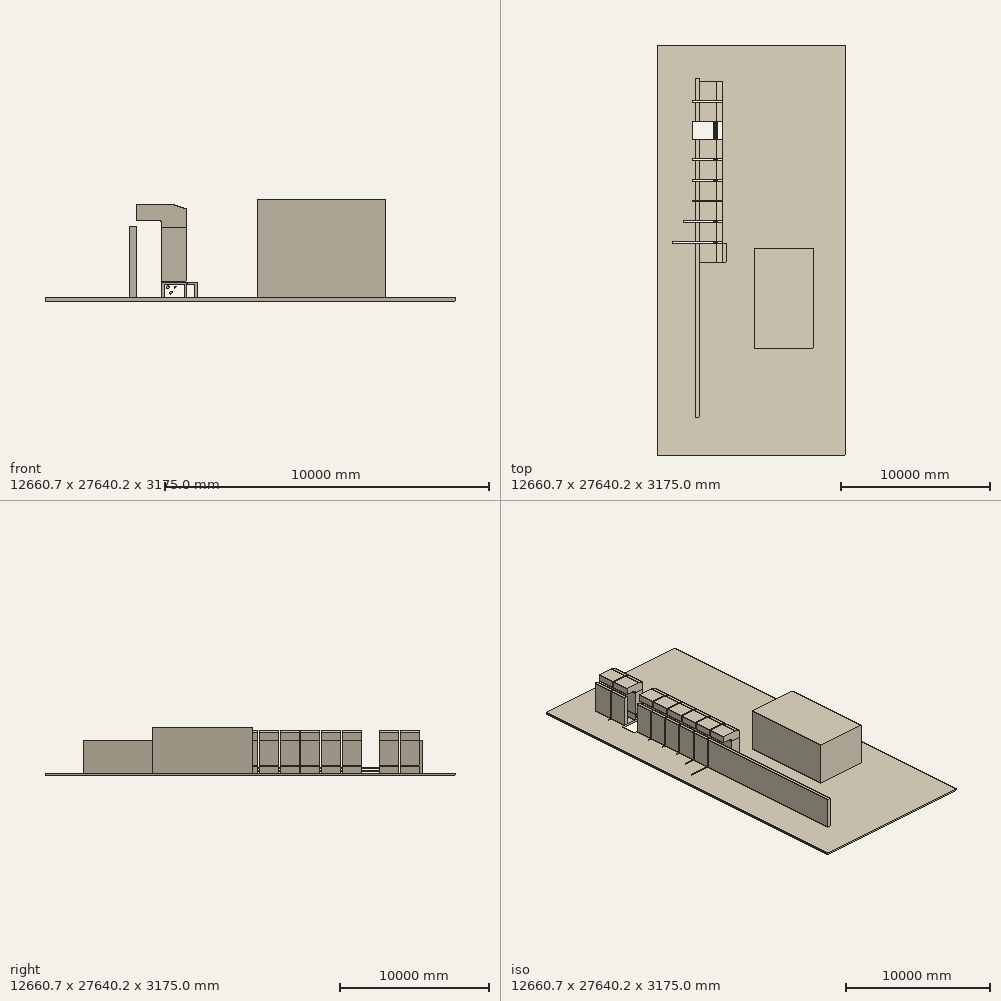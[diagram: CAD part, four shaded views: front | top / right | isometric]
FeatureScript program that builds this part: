
annotation { "Feature Type Name" : "Feature", "Feature Type Description" : "" }
export const myFeature = defineFeature(function(context is Context, id is Id, definition is map)
    precondition{}
    {
        {
            var Q0;
            Q0=qCreatedBy(makeId("Top.planeOp"),FACE);
            var sketch = newSketch(context, id + "F0", { "sketchPlane" : qUnion([Q0])});
            skLineSegment(sketch, "E0.bottom", {"start": v(0, 0) * mm, "end": v(3962.4, 0) * mm});
            skLineSegment(sketch, "E0.top", {"start": v(0, 9040.37) * mm, "end": v(100.58, 9040.37) * mm});
            skLineSegment(sketch, "E0.left", {"start": v(0, 0) * mm, "end": v(0, 9040.37) * mm});
            skLineSegment(sketch, "E0.right", {"start": v(3962.4, 0) * mm, "end": v(3962.4, 100.58) * mm});
            skLineSegment(sketch, "E1.bottom", {"start": v(0, -9144) * mm, "end": v(3962.4, -9144) * mm});
            skLineSegment(sketch, "E1.top", {"start": v(0, -2438.4) * mm, "end": v(3962.4, -2438.4) * mm});
            skLineSegment(sketch, "E1.left", {"start": v(0, -2438.4) * mm, "end": v(0, -9144) * mm});
            skLineSegment(sketch, "E1.right", {"start": v(3962.4, -2438.4) * mm, "end": v(3962.4, -9144) * mm});
            skLineSegment(sketch, "E2", {"start": v(100.58, 9040.37) * mm, "end": v(100.58, 100.58) * mm});
            skLineSegment(sketch, "E3", {"start": v(100.58, 100.58) * mm, "end": v(3962.4, 100.58) * mm});
            skSolve(sketch);
        }
        {
            var Q0;
            Q0=qSketchRegion(id+"F0",true);
            extrude(context, id + "F1", {"entities" : qUnion([Q0]), "depth" : 3048 * mm});
        }
        {
            var Q0;
            Q0=qCreatedBy(makeId("Top.planeOp"),FACE);
            var sketch = newSketch(context, id + "F2", { "sketchPlane" : qUnion([Q0])});
            skLineSegment(sketch, "E4.bottom", {"start": v(-3718.56, 9040.37) * mm, "end": v(3962.4, 9040.37) * mm});
            skLineSegment(sketch, "E4.top", {"start": v(-3718.56, 9284.2) * mm, "end": v(3962.4, 9284.2) * mm});
            skLineSegment(sketch, "E4.left", {"start": v(-3718.56, 9040.37) * mm, "end": v(-3718.56, 9284.2) * mm});
            skLineSegment(sketch, "E4.right", {"start": v(3962.4, 9040.37) * mm, "end": v(3962.4, 9284.2) * mm});
            skLineSegment(sketch, "E5.bottom", {"start": v(-3718.56, 9040.37) * mm, "end": v(-3962.4, 9040.37) * mm});
            skLineSegment(sketch, "E5.top", {"start": v(-3718.56, -13819.63) * mm, "end": v(-3962.4, -13819.63) * mm});
            skLineSegment(sketch, "E5.left", {"start": v(-3718.56, 9040.37) * mm, "end": v(-3718.56, -13819.63) * mm});
            skLineSegment(sketch, "E5.right", {"start": v(-3962.4, 9040.37) * mm, "end": v(-3962.4, -13819.63) * mm});
            skSolve(sketch);
        }
        {
            var Q0;
            Q0=qSketchRegion(id+"F2",true);
            extrude(context, id + "F3", {"entities" : qUnion([Q0]), "depth" : 2212.85 * mm});
        }
        {
            var Q0;
            Q0=makeQuery(id+"F1.opExtrude","CAP_FACE",FACE,{"disambiguationData":[OSD([sQuery(id+"F0.wireOp",EDGE,"E0.bottom"),sQuery(id+"F0.wireOp",EDGE,"E0.top"),sQuery(id+"F0.wireOp",EDGE,"E0.left"),sQuery(id+"F0.wireOp",EDGE,"E0.right")])],"isStart":false});
            var sketch = newSketch(context, id + "F4", { "sketchPlane" : qUnion([Q0])});
            skLineSegment(sketch, "E6.bottom", {"start": v(3962.4, 9284.2) * mm, "end": v(-2990.09, 9284.2) * mm});
            skLineSegment(sketch, "E6.top", {"start": v(3962.4, -10436.35) * mm, "end": v(-2990.09, -10436.35) * mm});
            skLineSegment(sketch, "E6.left", {"start": v(3962.4, 9284.2) * mm, "end": v(3962.4, -10436.35) * mm});
            skLineSegment(sketch, "E6.right", {"start": v(-2990.09, 9284.2) * mm, "end": v(-2990.09, -10436.35) * mm});
            skSolve(sketch);
        }
        {
            var Q0;
            Q0=qSketchRegion(id+"F4",true);
            extrude(context, id + "F5", {"entities" : qUnion([Q0]), "depth" : 1270 * mm});
        }
        {
            var Q0;
            Q0=makeQuery(id+"F1.opExtrude","SWEPT_FACE",FACE,{"disambiguationData":[OSD([sQuery(id+"F0.wireOp",EDGE,"E1.right")])]});
            var sketch = newSketch(context, id + "F6", { "sketchPlane" : qUnion([Q0])});
            skLineSegment(sketch, "E7.bottom", {"start": v(-9144, 0) * mm, "end": v(9284.2, 0) * mm});
            skLineSegment(sketch, "E7.top", {"start": v(-9144, 4318) * mm, "end": v(9284.2, 4318) * mm});
            skLineSegment(sketch, "E7.left", {"start": v(-9144, 0) * mm, "end": v(-9144, 3048) * mm});
            skLineSegment(sketch, "E7.right", {"start": v(9284.2, 0) * mm, "end": v(9284.2, 4318) * mm});
            skLineSegment(sketch, "E8.bottom", {"start": v(-9144, 4318) * mm, "end": v(-10436.35, 4318) * mm});
            skLineSegment(sketch, "E8.top", {"start": v(-9144, 3048) * mm, "end": v(-10436.35, 3048) * mm});
            skLineSegment(sketch, "E8.right", {"start": v(-10436.35, 4318) * mm, "end": v(-10436.35, 3048) * mm});
            skSolve(sketch);
        }
        {
            var Q0;
            Q0=qSketchRegion(id+"F6",true);
            extrude(context, id + "F7", {"entities" : qUnion([Q0]), "depth" : 1270 * mm});
        }
        {
            var Q0;
            Q0=qCreatedBy(makeId("Top.planeOp"),FACE);
            var sketch = newSketch(context, id + "F8", { "sketchPlane" : qUnion([Q0])});
            skLineSegment(sketch, "E9.bottom", {"start": v(6117.86, 11268.55) * mm, "end": v(-6542.87, 11268.55) * mm});
            skLineSegment(sketch, "E9.top", {"start": v(6117.86, -16371.62) * mm, "end": v(-6542.87, -16371.62) * mm});
            skLineSegment(sketch, "E9.left", {"start": v(6117.86, 11268.55) * mm, "end": v(6117.86, -16371.62) * mm});
            skLineSegment(sketch, "E9.right", {"start": v(-6542.87, 11268.55) * mm, "end": v(-6542.87, -16371.62) * mm});
            skSolve(sketch);
        }
        {
            var Q0;
            Q0=qSketchRegion(id+"F8",true);
            extrude(context, id + "F9", {"entities" : qUnion([Q0]), "oppositeDirection" : true, "depth" : 127 * mm});
        }
        {
            var Q0;
            Q0=makeQuery(id+"F3.opExtrude","CAP_FACE",FACE,{"disambiguationData":[OSD([sQuery(id+"F2.wireOp",EDGE,"E4.bottom"),sQuery(id+"F2.wireOp",EDGE,"E4.top"),sQuery(id+"F2.wireOp",EDGE,"E4.left"),sQuery(id+"F2.wireOp",EDGE,"E4.right")])],"isStart":false});
            var sketch = newSketch(context, id + "F10", { "sketchPlane" : qUnion([Q0])});
            skLineSegment(sketch, "E10.bottom", {"start": v(-3718.56, 9284.2) * mm, "end": v(3962.4, 9284.2) * mm});
            skLineSegment(sketch, "E10.top", {"start": v(-3718.56, 9040.37) * mm, "end": v(3962.4, 9040.37) * mm});
            skLineSegment(sketch, "E10.left", {"start": v(-3718.56, 9284.2) * mm, "end": v(-3718.56, 9040.37) * mm});
            skLineSegment(sketch, "E10.right", {"start": v(3962.4, 9284.2) * mm, "end": v(3962.4, 9040.37) * mm});
            skSolve(sketch);
        }
        {
            var Q0;
            Q0=qSketchRegion(id+"F10",true);
            var Q1;
            Q1=makeQuery(id+"F5.opExtrude","CAP_FACE",FACE,{"disambiguationData":[OSD([sQuery(id+"F4.wireOp",EDGE,"E6.bottom"),sQuery(id+"F4.wireOp",EDGE,"E6.top"),sQuery(id+"F4.wireOp",EDGE,"E6.left"),sQuery(id+"F4.wireOp",EDGE,"E6.right")])],"isStart":false});
            extrude(context, id + "F11", {"entities" : qUnion([Q0]), "operationType" : NewBodyOperationType.ADD, "endBound" : BoundingType.UP_TO_SURFACE, "endBoundEntityFace" : qUnion([Q1]), "depth" : 25.4 * mm});
        }
        {
            var Q0;
            Q0=qCreatedBy(makeId("Top.planeOp"),FACE);
            var sketch = newSketch(context, id + "F12", { "sketchPlane" : qUnion([Q0])});
            skLineSegment(sketch, "E11.bottom", {"start": v(-2956.56, -560.83) * mm, "end": v(-2181.86, -560.83) * mm});
            skLineSegment(sketch, "E11.top", {"start": v(-2956.56, 734.57) * mm, "end": v(-2181.86, 734.57) * mm});
            skLineSegment(sketch, "E11.left", {"start": v(-2956.56, -560.83) * mm, "end": v(-2956.56, 734.57) * mm});
            skLineSegment(sketch, "E11.right", {"start": v(-2181.86, -560.83) * mm, "end": v(-2181.86, 734.57) * mm});
            skLineSegment(sketch, "E12.bottom", {"start": v(-2956.56, 836.17) * mm, "end": v(-2181.86, 836.17) * mm});
            skLineSegment(sketch, "E12.top", {"start": v(-2956.56, 2131.57) * mm, "end": v(-2181.86, 2131.57) * mm});
            skLineSegment(sketch, "E12.left", {"start": v(-2956.56, 836.17) * mm, "end": v(-2956.56, 2131.57) * mm});
            skLineSegment(sketch, "E12.right", {"start": v(-2181.86, 836.17) * mm, "end": v(-2181.86, 2131.57) * mm});
            skLineSegment(sketch, "E13.bottom", {"start": v(-2956.56, 2233.17) * mm, "end": v(-2181.86, 2233.17) * mm});
            skLineSegment(sketch, "E13.top", {"start": v(-2956.56, 3528.57) * mm, "end": v(-2181.86, 3528.57) * mm});
            skLineSegment(sketch, "E13.left", {"start": v(-2956.56, 2233.17) * mm, "end": v(-2956.56, 3528.57) * mm});
            skLineSegment(sketch, "E13.right", {"start": v(-2181.86, 2233.17) * mm, "end": v(-2181.86, 3528.57) * mm});
            skLineSegment(sketch, "E14.bottom", {"start": v(-2956.56, 8837.17) * mm, "end": v(-2181.86, 8837.17) * mm});
            skLineSegment(sketch, "E14.top", {"start": v(-2956.56, 7541.77) * mm, "end": v(-2181.86, 7541.77) * mm});
            skLineSegment(sketch, "E14.left", {"start": v(-2956.56, 8837.17) * mm, "end": v(-2956.56, 7541.77) * mm});
            skLineSegment(sketch, "E14.right", {"start": v(-2181.86, 8837.17) * mm, "end": v(-2181.86, 7541.77) * mm});
            skLineSegment(sketch, "E15.bottom", {"start": v(-2956.56, 7440.17) * mm, "end": v(-2181.86, 7440.17) * mm});
            skLineSegment(sketch, "E15.top", {"start": v(-2956.56, 6144.77) * mm, "end": v(-2181.86, 6144.77) * mm});
            skLineSegment(sketch, "E15.left", {"start": v(-2956.56, 7440.17) * mm, "end": v(-2956.56, 6144.77) * mm});
            skLineSegment(sketch, "E15.right", {"start": v(-2181.86, 7440.17) * mm, "end": v(-2181.86, 6144.77) * mm});
            skLineSegment(sketch, "E16.bottom", {"start": v(-2956.56, 4925.57) * mm, "end": v(-2181.86, 4925.57) * mm});
            skLineSegment(sketch, "E16.top", {"start": v(-2956.56, 3630.17) * mm, "end": v(-2181.86, 3630.17) * mm});
            skLineSegment(sketch, "E16.left", {"start": v(-2956.56, 4925.57) * mm, "end": v(-2956.56, 3630.17) * mm});
            skLineSegment(sketch, "E16.right", {"start": v(-2181.86, 4925.57) * mm, "end": v(-2181.86, 3630.17) * mm});
            skLineSegment(sketch, "E17", {"start": v(-2956.56, 2131.57) * mm, "end": v(-2956.56, 2233.17) * mm, "construction": true});
            skLineSegment(sketch, "E18", {"start": v(-2956.56, 734.57) * mm, "end": v(-2956.56, 836.17) * mm, "construction": true});
            skLineSegment(sketch, "E19", {"start": v(-2956.56, 3528.57) * mm, "end": v(-2956.56, 3630.17) * mm, "construction": true});
            skLineSegment(sketch, "E20", {"start": v(-2956.56, 7440.17) * mm, "end": v(-2956.56, 7541.77) * mm, "construction": true});
            skLineSegment(sketch, "E21.bottom", {"start": v(-2956.56, -662.43) * mm, "end": v(-2181.86, -662.43) * mm});
            skLineSegment(sketch, "E21.top", {"start": v(-2956.56, -1957.83) * mm, "end": v(-2181.86, -1957.83) * mm});
            skLineSegment(sketch, "E21.left", {"start": v(-2956.56, -662.43) * mm, "end": v(-2956.56, -1957.83) * mm});
            skLineSegment(sketch, "E21.right", {"start": v(-2181.86, -662.43) * mm, "end": v(-2181.86, -1957.83) * mm});
            skLineSegment(sketch, "E22.bottom", {"start": v(-2956.56, -2059.43) * mm, "end": v(-2181.86, -2059.43) * mm});
            skLineSegment(sketch, "E22.top", {"start": v(-2956.56, -3354.83) * mm, "end": v(-2181.86, -3354.83) * mm});
            skLineSegment(sketch, "E22.left", {"start": v(-2956.56, -2059.43) * mm, "end": v(-2956.56, -3354.83) * mm});
            skLineSegment(sketch, "E22.right", {"start": v(-2181.86, -2059.43) * mm, "end": v(-2181.86, -3354.83) * mm});
            skLineSegment(sketch, "E23", {"start": v(-2956.56, -662.43) * mm, "end": v(-2956.56, -560.83) * mm, "construction": true});
            skLineSegment(sketch, "E24", {"start": v(-2956.56, -2059.43) * mm, "end": v(-2956.56, -1957.83) * mm, "construction": true});
            skSolve(sketch);
        }
        {
            var Q0;
            Q0=qSketchRegion(id+"F12",true);
            extrude(context, id + "F13", {"entities" : qUnion([Q0]), "depth" : 2184.4 * mm});
        }
        {
            var Q0;
            Q0=qCreatedBy(makeId("Top.planeOp"),FACE);
            var sketch = newSketch(context, id + "F14", { "sketchPlane" : qUnion([Q0])});
            skLineSegment(sketch, "E25.bottom", {"start": v(607.65, 7254.54) * mm, "end": v(3668.35, 7254.54) * mm});
            skLineSegment(sketch, "E25.top", {"start": v(607.65, 5165.39) * mm, "end": v(3668.35, 5165.39) * mm});
            skLineSegment(sketch, "E25.left", {"start": v(607.65, 7254.54) * mm, "end": v(607.65, 5165.39) * mm});
            skLineSegment(sketch, "E25.right", {"start": v(3668.35, 7254.54) * mm, "end": v(3668.35, 5165.39) * mm});
            skSolve(sketch);
        }
        {
            var Q0;
            Q0=qSketchRegion(id+"F14",true);
            extrude(context, id + "F15", {"entities" : qUnion([Q0]), "depth" : 1739.9 * mm});
        }
        {
            var Q0;
            Q0=qCreatedBy(makeId("Top.planeOp"),FACE);
            var sketch = newSketch(context, id + "F16", { "sketchPlane" : qUnion([Q0])});
            skLineSegment(sketch, "E26.bottom", {"start": v(1227.74, 8964) * mm, "end": v(478.44, 8964) * mm});
            skLineSegment(sketch, "E26.top", {"start": v(1227.74, 7363.8) * mm, "end": v(478.44, 7363.8) * mm});
            skLineSegment(sketch, "E26.left", {"start": v(1227.74, 8964) * mm, "end": v(1227.74, 7363.8) * mm});
            skLineSegment(sketch, "E26.right", {"start": v(478.44, 8964) * mm, "end": v(478.44, 7363.8) * mm});
            skSolve(sketch);
        }
        {
            var Q0;
            Q0=qSketchRegion(id+"F16",true);
            extrude(context, id + "F17", {"entities" : qUnion([Q0]), "depth" : 1447.8 * mm});
        }
        {
            var Q0;
            Q0=makeQuery(id+"F13.opExtrude","SWEPT_FACE",FACE,{"disambiguationData":[OSD([sQuery(id+"F12.wireOp",EDGE,"E22.top")])]});
            var sketch = newSketch(context, id + "F18", { "sketchPlane" : qUnion([Q0])});
            skLineSegment(sketch, "E27", {"start": v(-2956.56, 2184.4) * mm, "end": v(-2956.56, 2324.1) * mm});
            skLineSegment(sketch, "E28", {"start": v(-2956.56, 2324.1) * mm, "end": v(-3020.06, 2387.6) * mm});
            skLineSegment(sketch, "E29", {"start": v(-3020.06, 2387.6) * mm, "end": v(-3045.46, 2387.6) * mm});
            skLineSegment(sketch, "E30", {"start": v(-3045.46, 2387.6) * mm, "end": v(-3045.46, 2870.2) * mm, "construction": true});
            skLineSegment(sketch, "E31", {"start": v(-3045.46, 2870.2) * mm, "end": v(-2569.2, 2870.2) * mm});
            skLineSegment(sketch, "E32", {"start": v(-2569.2, 2870.2) * mm, "end": v(-2181.86, 2743.2) * mm});
            skLineSegment(sketch, "E33", {"start": v(-2181.86, 2743.2) * mm, "end": v(-2181.86, 2184.4) * mm});
            skLineSegment(sketch, "E34", {"start": v(-2181.86, 2184.4) * mm, "end": v(-2956.56, 2184.4) * mm});
            skLineSegment(sketch, "E35", {"start": v(-2569.2, 2870.2) * mm, "end": v(-2569.2, 2184.4) * mm, "construction": true});
            skLineSegment(sketch, "E36", {"start": v(-3045.46, 2387.6) * mm, "end": v(-3743.96, 2387.6) * mm});
            skLineSegment(sketch, "E37", {"start": v(-3743.96, 2387.6) * mm, "end": v(-3743.96, 2870.2) * mm});
            skLineSegment(sketch, "E38", {"start": v(-3743.96, 2870.2) * mm, "end": v(-3045.46, 2870.2) * mm});
            skSolve(sketch);
        }
        {
            var Q0;
            Q0 = qSketchRegion(id + "F18", true);
            var Q1;
            Q1=makeQuery(id+"F13.opExtrude","SWEPT_FACE",FACE,{"disambiguationData":[OSD([sQuery(id+"F12.wireOp",EDGE,"E14.bottom")])]});
            extrude(context, id + "F19", {"entities" : qUnion([Q0]), "endBound" : BoundingType.UP_TO_SURFACE, "oppositeDirection" : true, "endBoundEntityFace" : qUnion([Q1]), "depth" : 25.4 * mm});
        }
        {
            var Q0;
            Q0=makeQuery(id+"F19.opExtrude","SWEPT_FACE",FACE,{"disambiguationData":[OSD([sQuery(id+"F18.wireOp",EDGE,"E31"),sQuery(id+"F18.wireOp",EDGE,"zUbst6hV-jxuJ-IhWM-silx-YQ4qEfQ2v0dv")])]});
            var sketch = newSketch(context, id + "F20", { "sketchPlane" : qUnion([Q0])});
            skLineSegment(sketch, "E39.1", {"start": v(-2956.56, 734.57) * mm, "end": v(-2181.86, 734.57) * mm});
            skLineSegment(sketch, "E39.4", {"start": v(-2956.56, 836.17) * mm, "end": v(-2181.86, 836.17) * mm});
            skLineSegment(sketch, "E39.5", {"start": v(-2956.56, 2131.57) * mm, "end": v(-2181.86, 2131.57) * mm});
            skLineSegment(sketch, "E39.8", {"start": v(-2956.56, 2233.17) * mm, "end": v(-2181.86, 2233.17) * mm});
            skLineSegment(sketch, "E39.9", {"start": v(-2956.56, 3528.57) * mm, "end": v(-2181.86, 3528.57) * mm});
            skLineSegment(sketch, "E39.12", {"start": v(-2956.56, 8837.17) * mm, "end": v(-2181.86, 8837.17) * mm});
            skLineSegment(sketch, "E39.13", {"start": v(-2956.56, 7541.77) * mm, "end": v(-2181.86, 7541.77) * mm});
            skLineSegment(sketch, "E39.16", {"start": v(-2956.56, 7440.17) * mm, "end": v(-2181.86, 7440.17) * mm});
            skLineSegment(sketch, "E39.17", {"start": v(-2956.56, 6144.77) * mm, "end": v(-2181.86, 6144.77) * mm});
            skLineSegment(sketch, "E39.20", {"start": v(-2956.56, 4925.57) * mm, "end": v(-2181.86, 4925.57) * mm});
            skLineSegment(sketch, "E39.21", {"start": v(-2956.56, 3630.17) * mm, "end": v(-2181.86, 3630.17) * mm});
            skLineSegment(sketch, "E40", {"start": v(-2956.56, 734.57) * mm, "end": v(-4216.86, 734.57) * mm});
            skLineSegment(sketch, "E41", {"start": v(-4216.86, 734.57) * mm, "end": v(-4216.86, 836.17) * mm});
            skLineSegment(sketch, "E42", {"start": v(-4216.86, 836.17) * mm, "end": v(-2956.56, 836.17) * mm});
            skLineSegment(sketch, "E43", {"start": v(-2181.86, 734.57) * mm, "end": v(-2181.86, 836.17) * mm});
            skLineSegment(sketch, "E44", {"start": v(-2956.56, 2131.57) * mm, "end": v(-4216.86, 2131.57) * mm});
            skLineSegment(sketch, "E45", {"start": v(-4216.86, 2131.57) * mm, "end": v(-4216.86, 2233.17) * mm});
            skLineSegment(sketch, "E46", {"start": v(-4216.86, 2233.17) * mm, "end": v(-2956.56, 2233.17) * mm});
            skLineSegment(sketch, "E47", {"start": v(-2181.86, 2131.57) * mm, "end": v(-2181.86, 2233.17) * mm});
            skLineSegment(sketch, "E48", {"start": v(-2181.86, 3528.57) * mm, "end": v(-2181.86, 3630.17) * mm});
            skLineSegment(sketch, "E49", {"start": v(-2181.86, 4925.57) * mm, "end": v(-2181.86, 6144.77) * mm});
            skLineSegment(sketch, "E50", {"start": v(-2181.86, 7440.17) * mm, "end": v(-2181.86, 7541.77) * mm});
            skLineSegment(sketch, "E51", {"start": v(-2956.56, 3528.57) * mm, "end": v(-4216.86, 3528.57) * mm});
            skLineSegment(sketch, "E52", {"start": v(-4216.86, 3528.57) * mm, "end": v(-4216.86, 3630.17) * mm});
            skLineSegment(sketch, "E53", {"start": v(-4216.86, 3630.17) * mm, "end": v(-2956.56, 3630.17) * mm});
            skLineSegment(sketch, "E54", {"start": v(-2956.56, 4925.57) * mm, "end": v(-4216.86, 4925.57) * mm});
            skLineSegment(sketch, "E55", {"start": v(-4216.86, 4925.57) * mm, "end": v(-4216.86, 6144.77) * mm});
            skLineSegment(sketch, "E56", {"start": v(-4216.86, 6144.77) * mm, "end": v(-2956.56, 6144.77) * mm});
            skLineSegment(sketch, "E57", {"start": v(-2956.56, 7440.17) * mm, "end": v(-4216.86, 7440.17) * mm});
            skLineSegment(sketch, "E58", {"start": v(-4216.86, 7440.17) * mm, "end": v(-4216.86, 7541.77) * mm});
            skLineSegment(sketch, "E59", {"start": v(-4216.86, 7541.77) * mm, "end": v(-2956.56, 7541.77) * mm});
            skLineSegment(sketch, "E60.bottom", {"start": v(-2181.86, -560.83) * mm, "end": v(-4784.94, -560.83) * mm});
            skLineSegment(sketch, "E60.top", {"start": v(-2181.86, -662.43) * mm, "end": v(-4784.94, -662.43) * mm});
            skLineSegment(sketch, "E60.left", {"start": v(-2181.86, -560.83) * mm, "end": v(-2181.86, -662.43) * mm});
            skLineSegment(sketch, "E60.right", {"start": v(-4784.94, -560.83) * mm, "end": v(-4784.94, -662.43) * mm});
            skLineSegment(sketch, "E61.bottom", {"start": v(-2181.86, -1957.83) * mm, "end": v(-5549.38, -1957.83) * mm});
            skLineSegment(sketch, "E61.top", {"start": v(-2181.86, -2059.43) * mm, "end": v(-5549.38, -2059.43) * mm});
            skLineSegment(sketch, "E61.left", {"start": v(-2181.86, -1957.83) * mm, "end": v(-2181.86, -2059.43) * mm});
            skLineSegment(sketch, "E61.right", {"start": v(-5549.38, -1957.83) * mm, "end": v(-5549.38, -2059.43) * mm});
            skSolve(sketch);
        }
        {
            var Q0;
            Q0 = qSketchRegion(id + "F20", true);
            extrude(context, id + "F21", {"entities" : qUnion([Q0]), "operationType" : NewBodyOperationType.REMOVE, "endBound" : BoundingType.THROUGH_ALL, "oppositeDirection" : true, "depth" : 25.4 * mm});
        }
        {
            var Q0;
            Q0=qCreatedBy(makeId("Top.planeOp"),FACE);
            var sketch = newSketch(context, id + "F22", { "sketchPlane" : qUnion([Q0])});
            skSolve(sketch);
        }
        {
            var Q0;
            Q0 = qSketchRegion(id + "F22", true);
            var Q1;
            Q1=makeQuery(id+"F5.opExtrude","CAP_FACE",FACE,{"disambiguationData":[OSD([sQuery(id+"F4.wireOp",EDGE,"E6.bottom"),sQuery(id+"F4.wireOp",EDGE,"E6.top"),sQuery(id+"F4.wireOp",EDGE,"E6.left"),sQuery(id+"F4.wireOp",EDGE,"E6.right")])],"isStart":false});
            extrude(context, id + "F23", {"entities" : qUnion([Q0, Q1]), "depth" : 25.4 * mm});
        }
        {
            var Q0;
            Q0=makeQuery(id+"F13.opExtrude","SWEPT_FACE",FACE,{"disambiguationData":[OSD([sQuery(id+"F12.wireOp",EDGE,"E22.top")])]});
            var sketch = newSketch(context, id + "F24", { "sketchPlane" : qUnion([Q0])});
            skLineSegment(sketch, "E62.bottom", {"start": v(-2956.56, 488.95) * mm, "end": v(-2181.86, 488.95) * mm});
            skLineSegment(sketch, "E62.top", {"start": v(-2956.56, 482.6) * mm, "end": v(-2181.86, 482.6) * mm});
            skLineSegment(sketch, "E62.left", {"start": v(-2956.56, 488.95) * mm, "end": v(-2956.56, 482.6) * mm});
            skLineSegment(sketch, "E62.right", {"start": v(-2181.86, 488.95) * mm, "end": v(-2181.86, 482.6) * mm});
            skLineSegment(sketch, "E63.bottom", {"start": v(-2880.36, 406.4) * mm, "end": v(-2258.06, 406.4) * mm});
            skLineSegment(sketch, "E63.top", {"start": v(-2880.36, 0) * mm, "end": v(-2258.06, 0) * mm});
            skLineSegment(sketch, "E63.left", {"start": v(-2880.36, 406.4) * mm, "end": v(-2880.36, 0) * mm});
            skLineSegment(sketch, "E63.right", {"start": v(-2258.06, 406.4) * mm, "end": v(-2258.06, 0) * mm});
            skSolve(sketch);
        }
        {
            var Q0;
            Q0 = qSketchRegion(id + "F24", true);
            var Q1;
            Q1=makeQuery(id+"F13.opExtrude","SWEPT_FACE",FACE,{"disambiguationData":[OSD([sQuery(id+"F12.wireOp",EDGE,"E14.bottom")])]});
            extrude(context, id + "F25", {"entities" : qUnion([Q0]), "operationType" : NewBodyOperationType.REMOVE, "endBound" : BoundingType.UP_TO_SURFACE, "oppositeDirection" : true, "endBoundEntityFace" : qUnion([Q1]), "depth" : 25.4 * mm});
        }
        {
            var Q0;
            {var subQ2=sQuery(id+"F12.wireOp",EDGE,"E22.top");Q0=makeQuery(id+"F25.boolean.opBoolean","SPLIT",FACE,{"disambiguationData":[TD([makeQuery(id+"F25.opExtrude","SWEPT_FACE",FACE,{"disambiguationData":[OSD([sQuery(id+"F24.wireOp",EDGE,"E62.top")])]})])],"derivedFrom":makeQuery(id+"F13.opExtrude","SWEPT_FACE",FACE,{"disambiguationData":[OSD([subQ2])]})});}
            var sketch = newSketch(context, id + "F26", { "sketchPlane" : qUnion([Q0])});
            skCircle(sketch, "E64", {"center": v(-2755.23, 325.58) * mm, "radius": 44.3 * mm});
            skCircle(sketch, "E65", {"center": v(-2532.33, 324.26) * mm, "radius": 26.75 * mm});
            skCircle(sketch, "E66", {"center": v(-2659.35, 151) * mm, "radius": 40.42 * mm});
            skSolve(sketch);
        }
        {
            var Q0;
            Q0 = qSketchRegion(id + "F26", true);
            extrude(context, id + "F27", {"entities" : qUnion([Q0]), "oppositeDirection" : true, "depth" : 10160 * mm});
        }
        {
            var Q0;
            {var subQ2=sQuery(id+"F12.wireOp",EDGE,"E22.top");Q0=makeQuery(id+"F25.boolean.opBoolean","SPLIT",FACE,{"disambiguationData":[TD([makeQuery(id+"F25.opExtrude","SWEPT_FACE",FACE,{"disambiguationData":[OSD([sQuery(id+"F24.wireOp",EDGE,"E62.top")])]})])],"derivedFrom":makeQuery(id+"F13.opExtrude","SWEPT_FACE",FACE,{"disambiguationData":[OSD([subQ2])]})});}
            var sketch = newSketch(context, id + "F28", { "sketchPlane" : qUnion([Q0])});
            skLineSegment(sketch, "E67", {"start": v(-2169.16, 482.6) * mm, "end": v(-1864.36, 482.6) * mm});
            skLineSegment(sketch, "E68", {"start": v(-1864.36, 482.6) * mm, "end": v(-1864.36, 0) * mm});
            skLineSegment(sketch, "E69", {"start": v(-1864.36, 0) * mm, "end": v(-1940.56, 0) * mm});
            skLineSegment(sketch, "E70", {"start": v(-1940.56, 0) * mm, "end": v(-1940.56, 406.4) * mm});
            skLineSegment(sketch, "E71", {"start": v(-1940.56, 406.4) * mm, "end": v(-2169.16, 406.4) * mm});
            skLineSegment(sketch, "E72", {"start": v(-2169.16, 406.4) * mm, "end": v(-2169.16, 482.6) * mm});
            skSolve(sketch);
        }
        {
            var Q0;
            Q0 = qSketchRegion(id + "F28", true);
            var Q1;
            Q1=makeQuery(id+"F25.boolean.opBoolean","INTERSECT",VERTEX,{"disambiguationData":[OD(1.0)],"derivedFrom":[makeQuery(id+"F13.opExtrude","SWEPT_FACE",FACE,{"disambiguationData":[OSD([sQuery(id+"F12.wireOp",EDGE,"E22.bottom")])]}),makeQuery(id+"F25.opExtrude","SWEPT_FACE",FACE,{"disambiguationData":[OSD([sQuery(id+"F24.wireOp",EDGE,"E62.top")])]})]});
            extrude(context, id + "F29", {"entities" : qUnion([Q0]), "operationType" : NewBodyOperationType.ADD, "endBound" : BoundingType.UP_TO_VERTEX, "oppositeDirection" : true, "endBoundEntityVertex" : qUnion([Q1]), "depth" : 25.4 * mm});
        }
        {
            var Q0;
            Q0=makeQuery(id+"F1.opExtrude","SWEPT_BODY",BODY,{"disambiguationData":[OSD([sQuery(id+"F0.wireOp",EDGE,"E0.bottom"),sQuery(id+"F0.wireOp",EDGE,"E0.top"),sQuery(id+"F0.wireOp",EDGE,"E0.left"),sQuery(id+"F0.wireOp",EDGE,"E0.right"),sQuery(id+"F0.wireOp",EDGE,"E2"),sQuery(id+"F0.wireOp",EDGE,"E3")])]});
            var Q1;
            Q1=makeQuery(id+"F15.opExtrude","SWEPT_BODY",BODY,{"disambiguationData":[OSD([sQuery(id+"F14.wireOp",EDGE,"E25.bottom"),sQuery(id+"F14.wireOp",EDGE,"E25.top"),sQuery(id+"F14.wireOp",EDGE,"E25.left"),sQuery(id+"F14.wireOp",EDGE,"E25.right")])]});
            var Q2;
            Q2=makeQuery(id+"F23.opExtrude","SWEPT_BODY",BODY,{"disambiguationData":[OSD([sQuery(id+"F4.wireOp",EDGE,"E6.bottom"),sQuery(id+"F4.wireOp",EDGE,"E6.top"),sQuery(id+"F4.wireOp",EDGE,"E6.left"),sQuery(id+"F4.wireOp",EDGE,"E6.right")])]});
            var Q3;
            Q3=makeQuery(id+"F17.opExtrude","SWEPT_BODY",BODY,{"disambiguationData":[OSD([sQuery(id+"F16.wireOp",EDGE,"E26.bottom"),sQuery(id+"F16.wireOp",EDGE,"E26.top"),sQuery(id+"F16.wireOp",EDGE,"E26.left"),sQuery(id+"F16.wireOp",EDGE,"E26.right")])]});
            deleteBodies(context, id + "F30", {"entities" : qUnion([Q0, Q1, Q2, Q3])});
        }
    });
